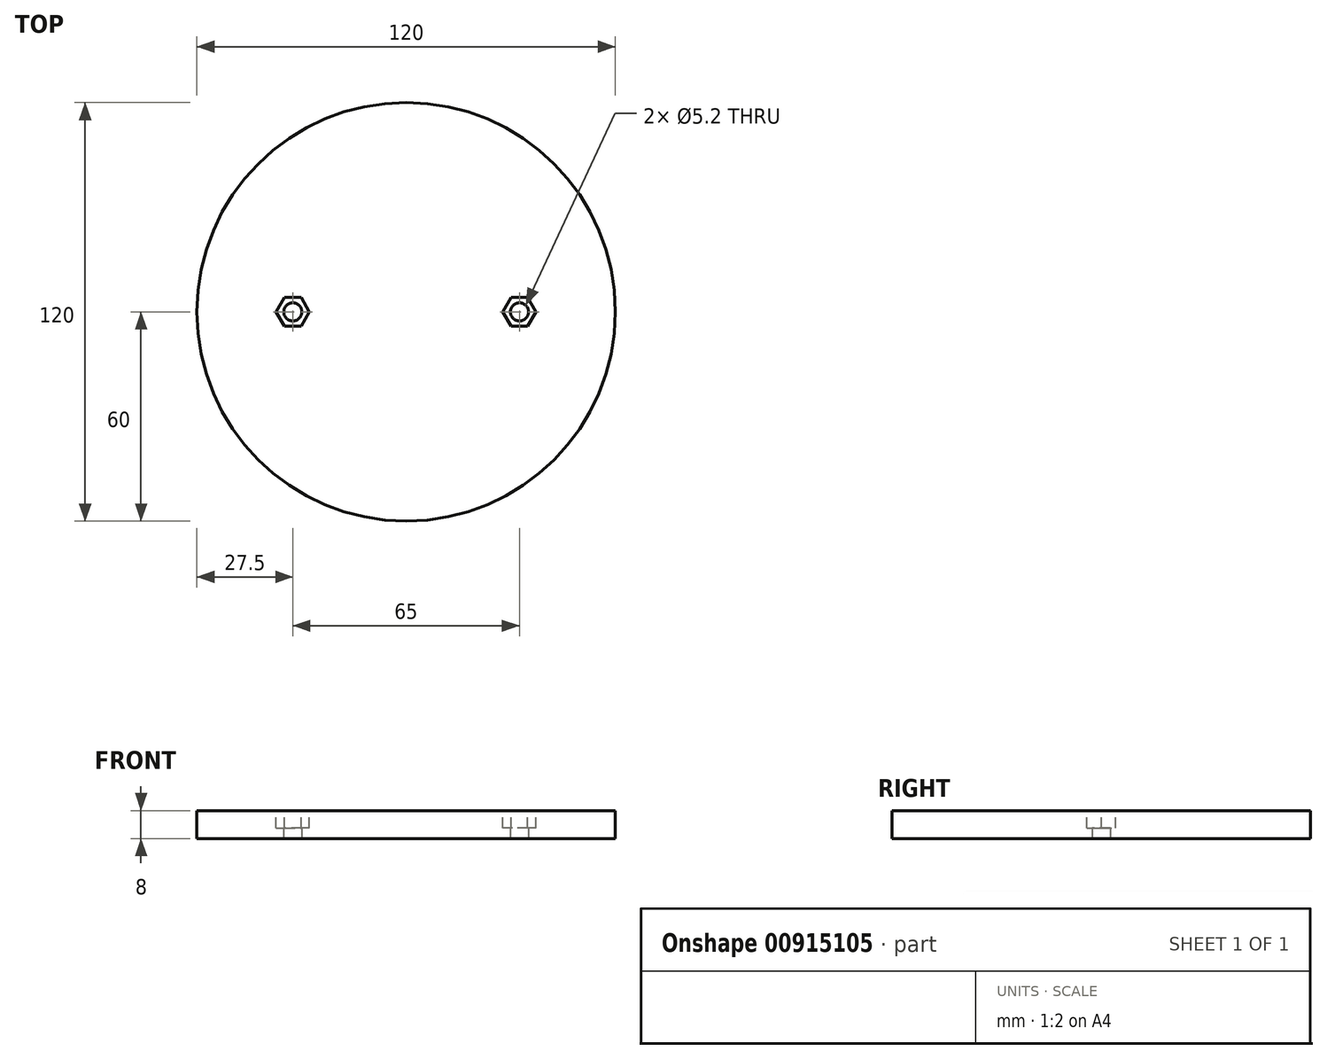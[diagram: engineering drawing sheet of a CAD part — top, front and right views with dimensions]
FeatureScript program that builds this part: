
annotation { "Feature Type Name" : "Feature", "Feature Type Description" : "" }
export const myFeature = defineFeature(function(context is Context, id is Id, definition is map)
    precondition{}
    {
        {
            var Q0;
            Q0=qCreatedBy(makeId("Top.planeOp"),FACE);
            var sketch = newSketch(context, id + "F0", { "sketchPlane" : qUnion([Q0])});
            skCircle(sketch, "E0", {"center": v(0, 0) * mm, "radius": 60 * mm});
            skCircle(sketch, "E1", {"center": v(-32.5, 0) * mm, "radius": 2.6 * mm});
            skCircle(sketch, "E2.MirrorC", {"center": v(32.5, 0) * mm, "radius": 2.6 * mm});
            skSolve(sketch);
        }
        {
            var Q0;
            Q0=makeQuery(id+"F0.imprint","IMPRINT",FACE,{"disambiguationData":[TD([[makeQuery(id+"F0.imprint","IMPRINT",EDGE,{"derivedFrom":sQuery(id+"F0.wireOp",EDGE,"E0")}),1.0]])]});
            extrude(context, id + "F1", {"entities" : qUnion([Q0]), "depth" : 8 * mm, "offsetDistance" : 25 * mm});
        }
        {
            var Q0;
            Q0=makeQuery(id+"F1.opExtrude","CAP_FACE",FACE,{"disambiguationData":[OSD([sQuery(id+"F0.wireOp",EDGE,"E0"),sQuery(id+"F0.wireOp",EDGE,"E1"),sQuery(id+"F0.wireOp",EDGE,"E2.MirrorC")])],"isStart":false});
            var sketch = newSketch(context, id + "F2", { "sketchPlane" : qUnion([Q0])});
            skCircle(sketch, "E3.cCircle", {"center": v(-32.5, 0) * mm, "radius": 4.12 * mm, "construction": true});
            skLineSegment(sketch, "E3.0", {"start": v(-34.88, 4.12) * mm, "end": v(-30.12, 4.12) * mm});
            skLineSegment(sketch, "E3.1", {"start": v(-30.12, 4.13) * mm, "end": v(-27.74, 0) * mm});
            skLineSegment(sketch, "E3.2", {"start": v(-27.74, 0) * mm, "end": v(-30.12, -4.12) * mm});
            skLineSegment(sketch, "E3.3", {"start": v(-30.12, -4.12) * mm, "end": v(-34.88, -4.13) * mm});
            skLineSegment(sketch, "E3.4", {"start": v(-34.88, -4.12) * mm, "end": v(-37.26, 0) * mm});
            skLineSegment(sketch, "E3.5", {"start": v(-37.26, 0) * mm, "end": v(-34.88, 4.12) * mm});
            skPoint(sketch, "E3.0.midPoint", {"position": v(-32.5, 4.12) * mm});
            skCircle(sketch, "E4.MirrorC", {"center": v(32.5, 0) * mm, "radius": 4.12 * mm, "construction": true});
            skLineSegment(sketch, "E5.MirrorCS", {"start": v(34.88, 4.12) * mm, "end": v(30.12, 4.12) * mm});
            skLineSegment(sketch, "E6.MirrorCS", {"start": v(30.12, 4.13) * mm, "end": v(27.74, 0) * mm});
            skLineSegment(sketch, "E7.MirrorCS", {"start": v(27.74, 0) * mm, "end": v(30.12, -4.12) * mm});
            skLineSegment(sketch, "E8.MirrorCS", {"start": v(30.12, -4.12) * mm, "end": v(34.88, -4.13) * mm});
            skLineSegment(sketch, "E9.MirrorCS", {"start": v(34.88, -4.12) * mm, "end": v(37.26, 0) * mm});
            skLineSegment(sketch, "E10.MirrorCS", {"start": v(37.26, 0) * mm, "end": v(34.88, 4.13) * mm});
            skSolve(sketch);
        }
        {
            var Q0;
            Q0=makeQuery(id+"F2.imprint","IMPRINT",FACE,{"disambiguationData":[TD([[makeQuery(id+"F2.imprint","IMPRINT",EDGE,{"derivedFrom":sQuery(id+"F2.wireOp",EDGE,"E5.MirrorCS")}),1.0]])]});
            var Q1;
            Q1=makeQuery(id+"F2.imprint","IMPRINT",FACE,{"disambiguationData":[TD([[makeQuery(id+"F2.imprint","IMPRINT",EDGE,{"derivedFrom":sQuery(id+"F2.wireOp",EDGE,"E3.0")}),-1.0]])]});
            extrude(context, id + "F3", {"entities" : qUnion([Q0, Q1]), "operationType" : NewBodyOperationType.REMOVE, "oppositeDirection" : true, "depth" : 5 * mm, "offsetDistance" : 25 * mm});
        }
    });
